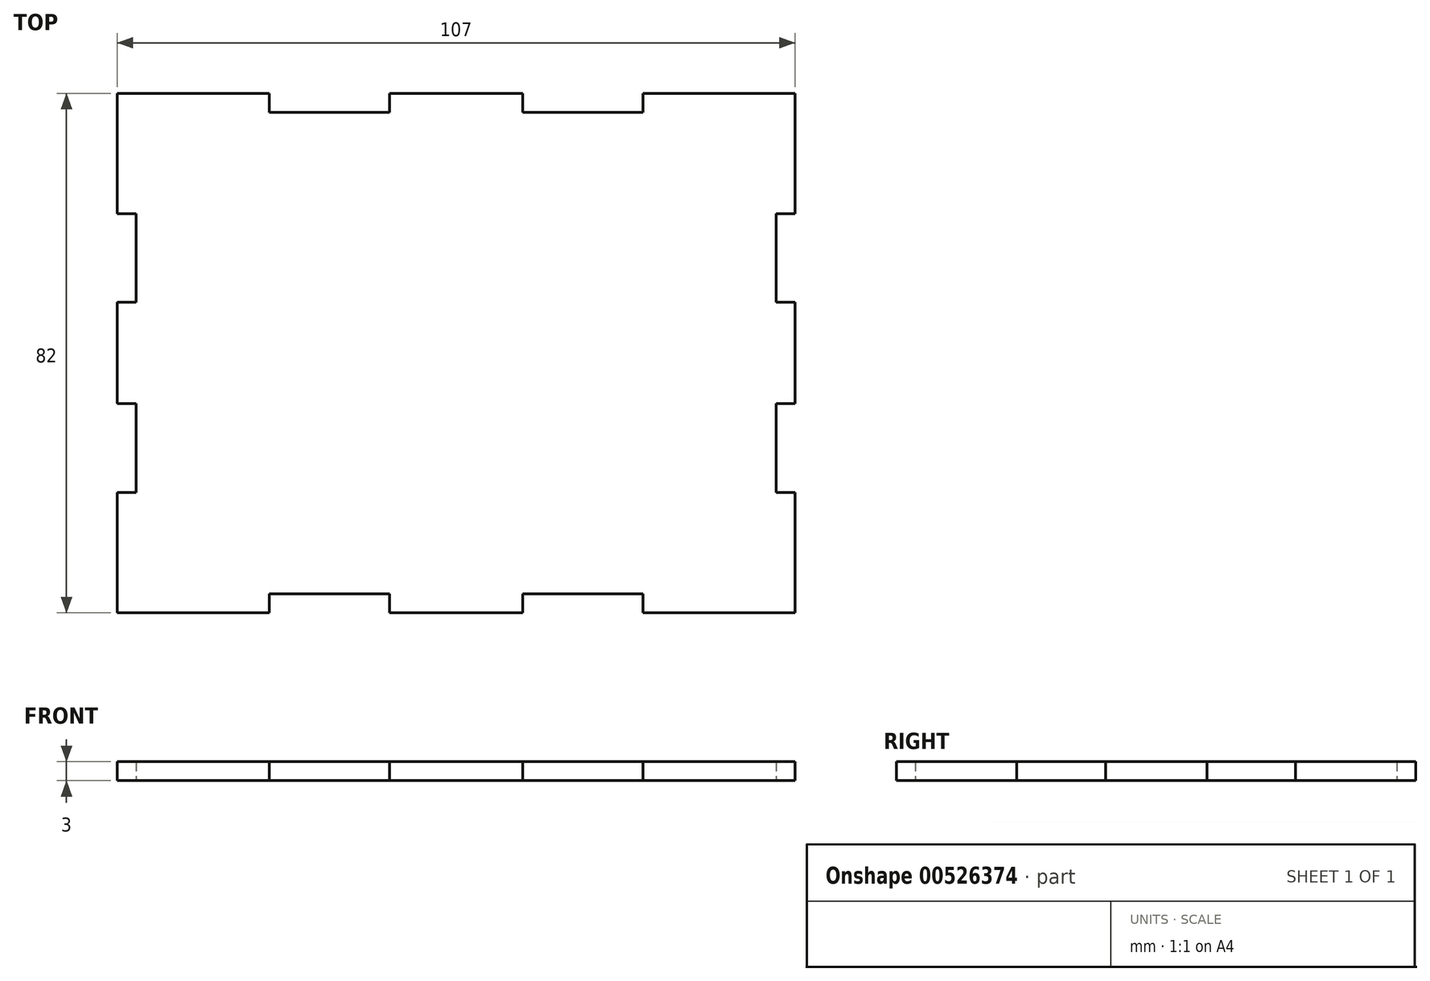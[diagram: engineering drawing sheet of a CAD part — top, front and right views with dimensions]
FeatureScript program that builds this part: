
annotation { "Feature Type Name" : "Feature", "Feature Type Description" : "" }
export const myFeature = defineFeature(function(context is Context, id is Id, definition is map)
    precondition{}
    {
        {
            assignVariable(context, id + "F0", {"name" : "thickness", "anyValue" : 3});
        }
        {
            var Q0;
            Q0=qCreatedBy(makeId("Top.planeOp"),FACE);
            var sketch = newSketch(context, id + "F1", { "sketchPlane" : qUnion([Q0])});
            skLineSegment(sketch, "E0", {"start": v(-50, 22.5) * mm, "end": v(-50, 7.5) * mm, "construction": true});
            skLineSegment(sketch, "E1", {"start": v(-50, 7.5) * mm, "end": v(-53, 7.5) * mm, "construction": true});
            skLineSegment(sketch, "E2", {"start": v(-53, 7.5) * mm, "end": v(-53, 0) * mm, "construction": true});
            skLineSegment(sketch, "E3", {"start": v(-10, 37.5) * mm, "end": v(-10, 40.5) * mm, "construction": true});
            skLineSegment(sketch, "E4", {"start": v(-10, 40.5) * mm, "end": v(0, 40.5) * mm, "construction": true});
            skLineSegment(sketch, "E5", {"start": v(-53, 40.5) * mm, "end": v(-53, 22.5) * mm, "construction": true});
            skLineSegment(sketch, "E6", {"start": v(-53, 22.5) * mm, "end": v(-50, 22.5) * mm, "construction": true});
            skLineSegment(sketch, "E7", {"start": v(-10, 37.5) * mm, "end": v(-30, 37.5) * mm, "construction": true});
            skLineSegment(sketch, "E8", {"start": v(-30, 37.5) * mm, "end": v(-30, 40.5) * mm, "construction": true});
            skLineSegment(sketch, "E9", {"start": v(-30, 40.5) * mm, "end": v(-53, 40.5) * mm, "construction": true});
            skLineSegment(sketch, "E10.MirrorCS", {"start": v(30, 37.5) * mm, "end": v(30, 40.5) * mm, "construction": true});
            skLineSegment(sketch, "E11.MirrorCS", {"start": v(10, 37.5) * mm, "end": v(10, 40.5) * mm, "construction": true});
            skLineSegment(sketch, "E12.MirrorCS", {"start": v(53, 22.5) * mm, "end": v(50, 22.5) * mm, "construction": true});
            skLineSegment(sketch, "E13.MirrorCS", {"start": v(50, 7.5) * mm, "end": v(53, 7.5) * mm, "construction": true});
            skLineSegment(sketch, "E14.MirrorCS", {"start": v(30, 40.5) * mm, "end": v(53, 40.5) * mm, "construction": true});
            skLineSegment(sketch, "E15.MirrorCS", {"start": v(53, 7.5) * mm, "end": v(53, 0) * mm, "construction": true});
            skLineSegment(sketch, "E16.MirrorCS", {"start": v(53, 40.5) * mm, "end": v(53, 22.5) * mm, "construction": true});
            skLineSegment(sketch, "E17.MirrorCS", {"start": v(10, 40.5) * mm, "end": v(0, 40.5) * mm, "construction": true});
            skLineSegment(sketch, "E18.MirrorCS", {"start": v(10, 37.5) * mm, "end": v(30, 37.5) * mm, "construction": true});
            skLineSegment(sketch, "E19.MirrorCS", {"start": v(50, 22.5) * mm, "end": v(50, 7.5) * mm, "construction": true});
            skLineSegment(sketch, "E20.MirrorCS", {"start": v(53, -7.5) * mm, "end": v(53, 0) * mm, "construction": true});
            skLineSegment(sketch, "E21.MirrorCS", {"start": v(-53, -7.5) * mm, "end": v(-53, 0) * mm, "construction": true});
            skLineSegment(sketch, "E22.MirrorCS", {"start": v(50, -7.5) * mm, "end": v(53, -7.5) * mm, "construction": true});
            skLineSegment(sketch, "E23.MirrorCS", {"start": v(-50, -7.5) * mm, "end": v(-53, -7.5) * mm, "construction": true});
            skLineSegment(sketch, "E24.MirrorCS", {"start": v(10, -37.5) * mm, "end": v(10, -40.5) * mm, "construction": true});
            skLineSegment(sketch, "E25.MirrorCS", {"start": v(-30, -37.5) * mm, "end": v(-30, -40.5) * mm, "construction": true});
            skLineSegment(sketch, "E26.MirrorCS", {"start": v(-10, -37.5) * mm, "end": v(-10, -40.5) * mm, "construction": true});
            skLineSegment(sketch, "E27.MirrorCS", {"start": v(30, -37.5) * mm, "end": v(30, -40.5) * mm, "construction": true});
            skLineSegment(sketch, "E28.MirrorCS", {"start": v(-53, -22.5) * mm, "end": v(-50, -22.5) * mm, "construction": true});
            skLineSegment(sketch, "E29.MirrorCS", {"start": v(53, -22.5) * mm, "end": v(50, -22.5) * mm, "construction": true});
            skLineSegment(sketch, "E30.MirrorCS", {"start": v(-10, -37.5) * mm, "end": v(-30, -37.5) * mm, "construction": true});
            skLineSegment(sketch, "E31.MirrorCS", {"start": v(-30, -40.5) * mm, "end": v(-53, -40.5) * mm, "construction": true});
            skLineSegment(sketch, "E32.MirrorCS", {"start": v(10, -40.5) * mm, "end": v(0, -40.5) * mm, "construction": true});
            skLineSegment(sketch, "E33.MirrorCS", {"start": v(-53, -40.5) * mm, "end": v(-53, -22.5) * mm, "construction": true});
            skLineSegment(sketch, "E34.MirrorCS", {"start": v(53, -40.5) * mm, "end": v(53, -22.5) * mm, "construction": true});
            skLineSegment(sketch, "E35.MirrorCS", {"start": v(30, -40.5) * mm, "end": v(53, -40.5) * mm, "construction": true});
            skLineSegment(sketch, "E36.MirrorCS", {"start": v(-50, -22.5) * mm, "end": v(-50, -7.5) * mm, "construction": true});
            skLineSegment(sketch, "E37.MirrorCS", {"start": v(10, -37.5) * mm, "end": v(30, -37.5) * mm, "construction": true});
            skLineSegment(sketch, "E38.MirrorCS", {"start": v(-10, -40.5) * mm, "end": v(0, -40.5) * mm, "construction": true});
            skLineSegment(sketch, "E39.MirrorCS", {"start": v(50, -22.5) * mm, "end": v(50, -7.5) * mm, "construction": true});
            skLineSegment(sketch, "E40.0", {"start": v(10.5, -38) * mm, "end": v(10.5, -41) * mm});
            skLineSegment(sketch, "E40.1", {"start": v(10.5, -38) * mm, "end": v(29.5, -38) * mm});
            skLineSegment(sketch, "E40.2", {"start": v(29.5, -38) * mm, "end": v(29.5, -41) * mm});
            skLineSegment(sketch, "E40.3", {"start": v(29.5, -41) * mm, "end": v(53.5, -41) * mm});
            skLineSegment(sketch, "E40.4", {"start": v(53.5, -41) * mm, "end": v(53.5, -22) * mm});
            skLineSegment(sketch, "E40.5", {"start": v(53.5, -22) * mm, "end": v(50.5, -22) * mm});
            skLineSegment(sketch, "E40.6", {"start": v(50.5, -22) * mm, "end": v(50.5, -8) * mm});
            skLineSegment(sketch, "E40.7", {"start": v(50.5, -8) * mm, "end": v(53.5, -8) * mm});
            skLineSegment(sketch, "E40.8", {"start": v(53.5, -8) * mm, "end": v(53.5, 0) * mm});
            skLineSegment(sketch, "E40.9", {"start": v(53.5, 8) * mm, "end": v(53.5, 0) * mm});
            skLineSegment(sketch, "E40.10", {"start": v(50.5, 8) * mm, "end": v(53.5, 8) * mm});
            skLineSegment(sketch, "E40.11", {"start": v(10.5, -41) * mm, "end": v(0, -41) * mm});
            skLineSegment(sketch, "E40.12", {"start": v(50.5, 22) * mm, "end": v(50.5, 8) * mm});
            skLineSegment(sketch, "E40.13", {"start": v(53.5, 22) * mm, "end": v(50.5, 22) * mm});
            skLineSegment(sketch, "E40.14", {"start": v(53.5, 41) * mm, "end": v(53.5, 22) * mm});
            skLineSegment(sketch, "E40.15", {"start": v(29.5, 41) * mm, "end": v(53.5, 41) * mm});
            skLineSegment(sketch, "E40.16", {"start": v(29.5, 38) * mm, "end": v(29.5, 41) * mm});
            skLineSegment(sketch, "E40.17", {"start": v(10.5, 38) * mm, "end": v(29.5, 38) * mm});
            skLineSegment(sketch, "E40.18", {"start": v(-53.5, -8) * mm, "end": v(-53.5, 0) * mm});
            skLineSegment(sketch, "E40.19", {"start": v(-50.5, -8) * mm, "end": v(-53.5, -8) * mm});
            skLineSegment(sketch, "E40.20", {"start": v(-50.5, -22) * mm, "end": v(-50.5, -8) * mm});
            skLineSegment(sketch, "E40.21", {"start": v(-53.5, -22) * mm, "end": v(-50.5, -22) * mm});
            skLineSegment(sketch, "E40.22", {"start": v(-53.5, -41) * mm, "end": v(-53.5, -22) * mm});
            skLineSegment(sketch, "E40.23", {"start": v(-29.5, -41) * mm, "end": v(-53.5, -41) * mm});
            skLineSegment(sketch, "E40.24", {"start": v(-10.5, -41) * mm, "end": v(0, -41) * mm});
            skLineSegment(sketch, "E40.25", {"start": v(-10.5, -38) * mm, "end": v(-10.5, -41) * mm});
            skLineSegment(sketch, "E40.26", {"start": v(-10.5, -38) * mm, "end": v(-29.5, -38) * mm});
            skLineSegment(sketch, "E40.27", {"start": v(-29.5, -38) * mm, "end": v(-29.5, -41) * mm});
            skLineSegment(sketch, "E40.28", {"start": v(-53.5, 8) * mm, "end": v(-53.5, 0) * mm});
            skLineSegment(sketch, "E40.29", {"start": v(-50.5, 8) * mm, "end": v(-53.5, 8) * mm});
            skLineSegment(sketch, "E40.30", {"start": v(-50.5, 22) * mm, "end": v(-50.5, 8) * mm});
            skLineSegment(sketch, "E40.31", {"start": v(-53.5, 22) * mm, "end": v(-50.5, 22) * mm});
            skLineSegment(sketch, "E40.32", {"start": v(-53.5, 41) * mm, "end": v(-53.5, 22) * mm});
            skLineSegment(sketch, "E40.33", {"start": v(-29.5, 41) * mm, "end": v(-53.5, 41) * mm});
            skLineSegment(sketch, "E40.34", {"start": v(-29.5, 38) * mm, "end": v(-29.5, 41) * mm});
            skLineSegment(sketch, "E40.35", {"start": v(-10.5, 38) * mm, "end": v(-29.5, 38) * mm});
            skLineSegment(sketch, "E40.36", {"start": v(-10.5, 38) * mm, "end": v(-10.5, 41) * mm});
            skLineSegment(sketch, "E40.37", {"start": v(-10.5, 41) * mm, "end": v(0, 41) * mm});
            skLineSegment(sketch, "E40.38", {"start": v(10.5, 41) * mm, "end": v(0, 41) * mm});
            skLineSegment(sketch, "E40.39", {"start": v(10.5, 38) * mm, "end": v(10.5, 41) * mm});
            skSolve(sketch);
        }
        {
            var Q0;
            Q0=makeQuery(id+"F1.imprint","IMPRINT",FACE,{"disambiguationData":[TD([[makeQuery(id+"F1.imprint","IMPRINT",EDGE,{"derivedFrom":sQuery(id+"F1.wireOp",EDGE,"E40.0")}),-1.0]])]});
            extrude(context, id + "F2", {"entities" : qUnion([Q0]), "depth" : (getVariable(context, 'thickness')) * mm, "offsetDistance" : 25 * mm});
        }
    });
